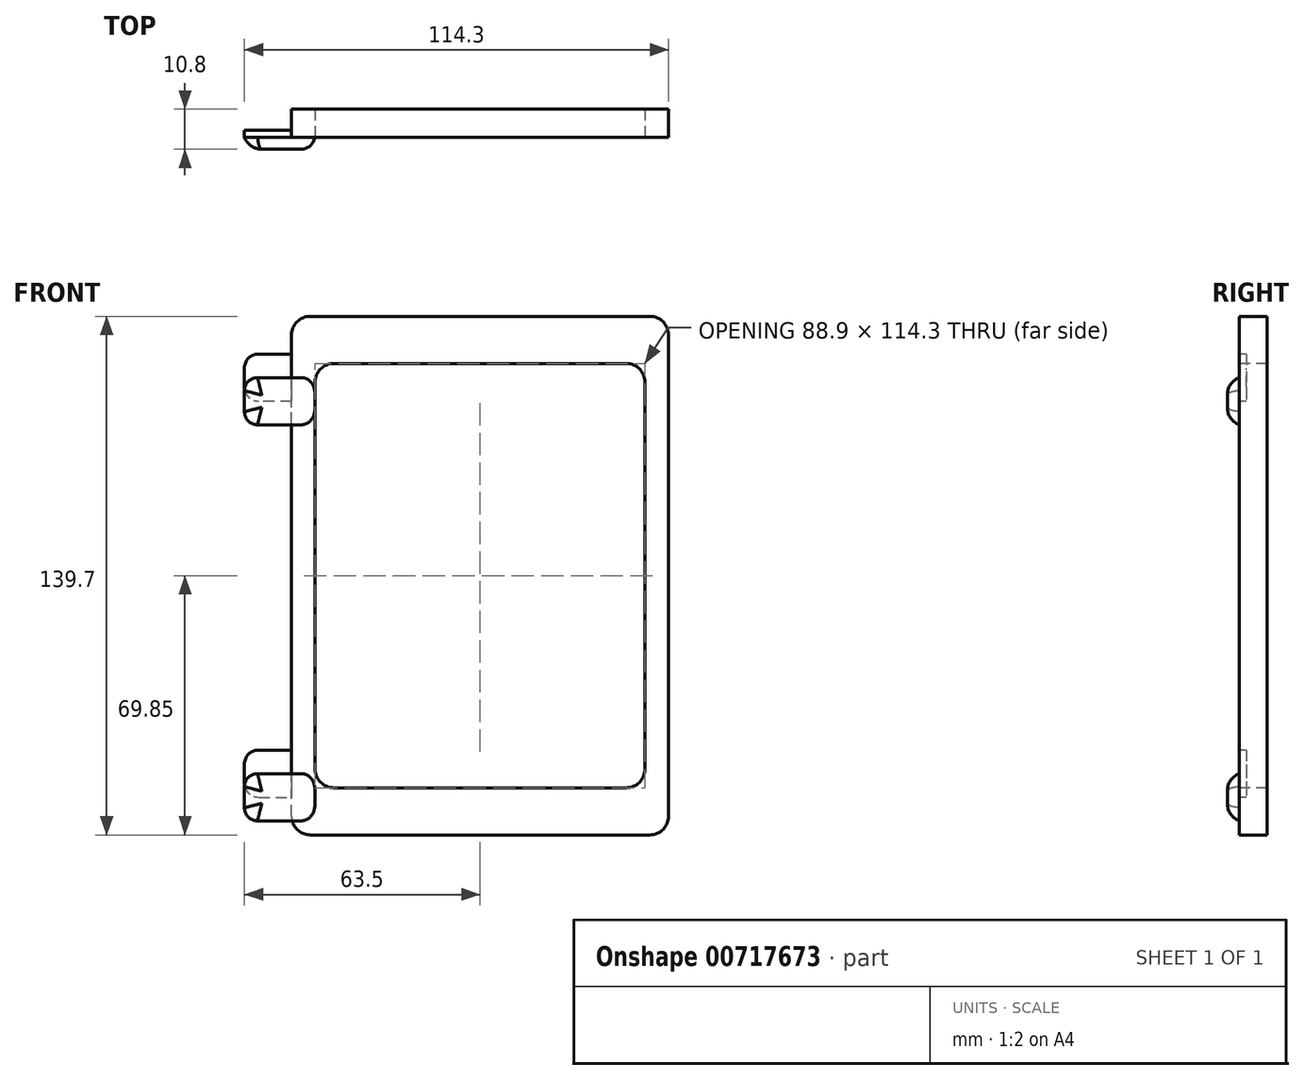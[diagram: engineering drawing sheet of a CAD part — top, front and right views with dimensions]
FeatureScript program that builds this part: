
annotation { "Feature Type Name" : "Feature", "Feature Type Description" : "" }
export const myFeature = defineFeature(function(context is Context, id is Id, definition is map)
    precondition{}
    {
        {
            var Q0;
            Q0=qCreatedBy(makeId("Front.planeOp"),FACE);
            var sketch = newSketch(context, id + "F0", { "sketchPlane" : qUnion([Q0])});
            skLineSegment(sketch, "E0.bottom", {"start": v(50.8, 69.85) * mm, "end": v(-50.8, 69.85) * mm});
            skLineSegment(sketch, "E0.top", {"start": v(50.8, -69.85) * mm, "end": v(-50.8, -69.85) * mm});
            skLineSegment(sketch, "E0.left", {"start": v(50.8, 69.85) * mm, "end": v(50.8, -69.85) * mm});
            skPoint(sketch, "E0.middle", {"position": v(0, 0) * mm});
            skLineSegment(sketch, "E1.bottom", {"start": v(44.45, 57.15) * mm, "end": v(-44.45, 57.15) * mm});
            skLineSegment(sketch, "E1.top", {"start": v(44.45, -57.15) * mm, "end": v(-44.45, -57.15) * mm});
            skLineSegment(sketch, "E1.left", {"start": v(44.45, 57.15) * mm, "end": v(44.45, -57.15) * mm});
            skLineSegment(sketch, "E2.bottom", {"start": v(-50.8, 47) * mm, "end": v(-63.5, 47) * mm});
            skLineSegment(sketch, "E2.top", {"start": v(-50.8, 59.7) * mm, "end": v(-63.5, 59.7) * mm});
            skLineSegment(sketch, "E2.right", {"start": v(-63.5, 47) * mm, "end": v(-63.5, 59.7) * mm});
            skLineSegment(sketch, "E3.bottom", {"start": v(-63.5, -46.99) * mm, "end": v(-50.8, -46.99) * mm});
            skLineSegment(sketch, "E3.top", {"start": v(-63.5, -59.69) * mm, "end": v(-50.8, -59.69) * mm});
            skPoint(sketch, "E4", {"position": v(-57.15, 53.34) * mm});
            skPoint(sketch, "E5", {"position": v(-57.15, -53.34) * mm});
            skLineSegment(sketch, "E6", {"start": v(-50.8, 59.7) * mm, "end": v(-50.8, 69.85) * mm});
            skLineSegment(sketch, "E7", {"start": v(-50.8, 47) * mm, "end": v(-50.8, -46.99) * mm});
            skLineSegment(sketch, "E8", {"start": v(-50.8, -59.69) * mm, "end": v(-50.8, -69.85) * mm});
            skLineSegment(sketch, "E9", {"start": v(-44.45, 57.15) * mm, "end": v(-44.45, -57.15) * mm});
            skLineSegment(sketch, "E10.bottom", {"start": v(-63.5, 59.7) * mm, "end": v(-45.72, 59.7) * mm});
            skLineSegment(sketch, "E10.top", {"start": v(-50.8, 47) * mm, "end": v(-45.72, 47) * mm});
            skLineSegment(sketch, "E10.right", {"start": v(-45.72, 59.7) * mm, "end": v(-45.72, 47) * mm});
            skLineSegment(sketch, "E11.bottom", {"start": v(-63.5, -46.99) * mm, "end": v(-45.72, -46.99) * mm});
            skLineSegment(sketch, "E11.top", {"start": v(-63.5, -59.69) * mm, "end": v(-45.72, -59.69) * mm});
            skLineSegment(sketch, "E11.left", {"start": v(-63.5, -46.99) * mm, "end": v(-63.5, -59.69) * mm});
            skLineSegment(sketch, "E11.right", {"start": v(-45.72, -46.99) * mm, "end": v(-45.72, -59.69) * mm});
            skLineSegment(sketch, "E12", {"start": v(-50.8, 59.7) * mm, "end": v(-50.8, 47) * mm});
            skLineSegment(sketch, "E13", {"start": v(-50.8, -46.99) * mm, "end": v(-50.8, -59.69) * mm});
            skSolve(sketch);
        }
        {
            var Q0;
            Q0=makeQuery(id+"F0.imprint","IMPRINT",FACE,{"disambiguationData":[TD([[makeQuery(id+"F0.imprint","IMPRINT",EDGE,{"derivedFrom":sQuery(id+"F0.wireOp",EDGE,"E0.bottom")}),1.0]])]});
            var Q1;
            {var subQ2=sQuery(id+"F0.wireOp",EDGE,"E10.right");Q1=makeQuery(id+"F0.imprint","IMPRINT",FACE,{"disambiguationData":[TD([[makeQuery(id+"F0.imprint","IMPRINT",EDGE,{"derivedFrom":subQ2}),-1.0]])]});}
            var Q2;
            {var subQ2=sQuery(id+"F0.wireOp",EDGE,"E11.right");Q2=makeQuery(id+"F0.imprint","IMPRINT",FACE,{"disambiguationData":[TD([[makeQuery(id+"F0.imprint","IMPRINT",EDGE,{"derivedFrom":subQ2}),-1.0]])]});}
            extrude(context, id + "F1", {"entities" : qUnion([Q0, Q1, Q2]), "depth" : -7.62 * mm, "offsetDistance" : 25.4 * mm});
        }
        {
            var Q0;
            {var subQ0=sQuery(id+"F0.wireOp",EDGE,"E2.right");Q0=makeQuery(id+"F0.imprint","IMPRINT",FACE,{"disambiguationData":[TD([[makeQuery(id+"F0.imprint","IMPRINT",EDGE,{"derivedFrom":subQ0}),-1.0]])]});}
            var Q1;
            {var subQ2=sQuery(id+"F0.wireOp",EDGE,"E11.left");Q1=makeQuery(id+"F0.imprint","IMPRINT",FACE,{"disambiguationData":[TD([[makeQuery(id+"F0.imprint","IMPRINT",EDGE,{"derivedFrom":subQ2}),1.0]])]});}
            extrude(context, id + "F2", {"entities" : qUnion([Q0, Q1]), "depth" : -1.9 * mm, "offsetDistance" : 25.4 * mm});
        }
        {
            var Q0;
            Q0=sQuery(id+"F0.wireOp",VERTEX,"E4");
            var Q1;
            Q1=sQuery(id+"F0.wireOp",VERTEX,"E5");
            var Q2;
            Q2=makeQuery(id+"F2.opExtrude","SWEPT_BODY",BODY,{"disambiguationData":[OSD([sQuery(id+"F0.wireOp",EDGE,"E2.right"),sQuery(id+"F0.wireOp",EDGE,"E10.bottom"),sQuery(id+"F0.wireOp",EDGE,"E10.top"),sQuery(id+"F0.wireOp",EDGE,"E12")])]});
            var Q3;
            Q3=makeQuery(id+"F2.opExtrude","SWEPT_BODY",BODY,{"disambiguationData":[OSD([sQuery(id+"F0.wireOp",EDGE,"E11.bottom"),sQuery(id+"F0.wireOp",EDGE,"E11.top"),sQuery(id+"F0.wireOp",EDGE,"E11.left"),sQuery(id+"F0.wireOp",EDGE,"E13")])]});
            hole(context, id + "F3", {"style" : HoleStyle.SIMPLE, "endStyle" : HoleEndStyle.THROUGH, "oppositeDirection" : true, "holeDiameter" : 2.97 * mm, "majorDiameter" : 6.35 * mm, "isTappedThrough" : true, "tappedDepth" : 12.7 * mm, "tapClearance" : 3, "locations" : qUnion([Q0, Q1]), "scope" : qUnion([Q2, Q3])});
        }
        {
            var Q0;
            Q0=makeQuery(id+"F1.opExtrude","SWEPT_EDGE",EDGE,{"disambiguationData":[OSD([sQuery(id+"F0.wireOp",EDGE,"E0.bottom"),sQuery(id+"F0.wireOp",EDGE,"E0.left")])]});
            var Q1;
            Q1=makeQuery(id+"F1.opExtrude","SWEPT_EDGE",EDGE,{"disambiguationData":[OSD([sQuery(id+"F0.wireOp",EDGE,"E0.top"),sQuery(id+"F0.wireOp",EDGE,"E0.left")])]});
            var Q2;
            Q2=makeQuery(id+"F1.opExtrude","SWEPT_EDGE",EDGE,{"disambiguationData":[OSD([sQuery(id+"F0.wireOp",EDGE,"E0.bottom"),sQuery(id+"F0.wireOp",EDGE,"E0.right")])]});
            var Q3;
            Q3=makeQuery(id+"F1.opExtrude","SWEPT_EDGE",EDGE,{"disambiguationData":[OSD([sQuery(id+"F0.wireOp",EDGE,"E0.top"),sQuery(id+"F0.wireOp",EDGE,"E0.right")])]});
            fillet(context, id + "F4", {"entities" : qUnion([Q0, Q1, Q2, Q3]), "radius" : 5.08 * mm, "tangentPropagation" : true, "allowEdgeOverflow" : false});
        }
        {
            var Q0;
            Q0=makeQuery(id+"F2.opExtrude","SWEPT_EDGE",EDGE,{"disambiguationData":[OSD([sQuery(id+"F0.wireOp",EDGE,"E2.right"),sQuery(id+"F0.wireOp",EDGE,"E10.bottom")])]});
            var Q1;
            Q1=makeQuery(id+"F2.opExtrude","SWEPT_EDGE",EDGE,{"disambiguationData":[OSD([sQuery(id+"F0.wireOp",EDGE,"E2.right"),sQuery(id+"F0.wireOp",EDGE,"E10.top")])]});
            var Q2;
            Q2=makeQuery(id+"F2.opExtrude","SWEPT_EDGE",EDGE,{"disambiguationData":[OSD([sQuery(id+"F0.wireOp",EDGE,"E11.bottom"),sQuery(id+"F0.wireOp",EDGE,"E11.left")])]});
            var Q3;
            Q3=makeQuery(id+"F2.opExtrude","SWEPT_EDGE",EDGE,{"disambiguationData":[OSD([sQuery(id+"F0.wireOp",EDGE,"E11.top"),sQuery(id+"F0.wireOp",EDGE,"E11.left")])]});
            fillet(context, id + "F5", {"entities" : qUnion([Q0, Q1, Q2, Q3]), "radius" : 3.8 * mm, "tangentPropagation" : true, "allowEdgeOverflow" : false});
        }
        {
            var Q0;
            Q0=makeQuery(id+"F1.opExtrude","SWEPT_EDGE",EDGE,{"disambiguationData":[OSD([sQuery(id+"F0.wireOp",EDGE,"E1.bottom"),sQuery(id+"F0.wireOp",EDGE,"E1.right")])]});
            var Q1;
            Q1=makeQuery(id+"F1.opExtrude","SWEPT_EDGE",EDGE,{"disambiguationData":[OSD([sQuery(id+"F0.wireOp",EDGE,"E1.top"),sQuery(id+"F0.wireOp",EDGE,"E1.right")])]});
            var Q2;
            Q2=makeQuery(id+"F1.opExtrude","SWEPT_EDGE",EDGE,{"disambiguationData":[OSD([sQuery(id+"F0.wireOp",EDGE,"E1.bottom"),sQuery(id+"F0.wireOp",EDGE,"E1.left")])]});
            var Q3;
            Q3=makeQuery(id+"F1.opExtrude","SWEPT_EDGE",EDGE,{"disambiguationData":[OSD([sQuery(id+"F0.wireOp",EDGE,"E1.top"),sQuery(id+"F0.wireOp",EDGE,"E1.left")])]});
            fillet(context, id + "F6", {"entities" : qUnion([Q0, Q1, Q2, Q3]), "radius" : 5.08 * mm, "tangentPropagation" : true, "allowEdgeOverflow" : false});
        }
        {
            var Q0;
            Q0=qCreatedBy(makeId("Front.planeOp"),FACE);
            var sketch = newSketch(context, id + "F7", { "sketchPlane" : qUnion([Q0])});
            skLineSegment(sketch, "E14.bottom", {"start": v(-63.5, 53.34) * mm, "end": v(-44.45, 53.34) * mm});
            skLineSegment(sketch, "E14.top", {"start": v(-63.5, 40.64) * mm, "end": v(-44.45, 40.64) * mm});
            skLineSegment(sketch, "E14.left", {"start": v(-63.5, 53.34) * mm, "end": v(-63.5, 40.64) * mm});
            skLineSegment(sketch, "E14.right", {"start": v(-44.45, 53.34) * mm, "end": v(-44.45, 40.64) * mm});
            skLineSegment(sketch, "E15.bottom", {"start": v(-63.5, -53.34) * mm, "end": v(-44.45, -53.34) * mm});
            skLineSegment(sketch, "E15.top", {"start": v(-63.5, -66.04) * mm, "end": v(-44.45, -66.04) * mm});
            skLineSegment(sketch, "E15.left", {"start": v(-63.5, -53.34) * mm, "end": v(-63.5, -66.04) * mm});
            skLineSegment(sketch, "E15.right", {"start": v(-44.45, -53.34) * mm, "end": v(-44.45, -66.04) * mm});
            skPoint(sketch, "E16", {"position": v(-57.15, 53.34) * mm});
            skPoint(sketch, "E17", {"position": v(-57.15, -59.69) * mm});
            skSolve(sketch);
        }
        {
            var Q0;
            Q0=makeQuery(id+"F7.imprint","IMPRINT",FACE,{"disambiguationData":[TD([[makeQuery(id+"F7.imprint","IMPRINT",EDGE,{"derivedFrom":sQuery(id+"F7.wireOp",EDGE,"E15.bottom")}),-1.0]])]});
            var Q1;
            Q1=makeQuery(id+"F7.imprint","IMPRINT",FACE,{"disambiguationData":[TD([[makeQuery(id+"F7.imprint","IMPRINT",EDGE,{"derivedFrom":sQuery(id+"F7.wireOp",EDGE,"E14.bottom")}),-1.0]])]});
            extrude(context, id + "F8", {"entities" : qUnion([Q0, Q1]), "depth" : 3.17 * mm, "offsetDistance" : 25.4 * mm});
        }
        {
            var Q0;
            Q0=makeQuery(id+"F8.opExtrude","CAP_EDGE",EDGE,{"disambiguationData":[OSD([sQuery(id+"F7.wireOp",EDGE,"E14.left")])],"isStart":false});
            var Q1;
            Q1=makeQuery(id+"F8.opExtrude","CAP_EDGE",EDGE,{"disambiguationData":[OSD([sQuery(id+"F7.wireOp",EDGE,"E14.bottom")])],"isStart":false});
            var Q2;
            Q2=makeQuery(id+"F8.opExtrude","CAP_EDGE",EDGE,{"disambiguationData":[OSD([sQuery(id+"F7.wireOp",EDGE,"E14.top")])],"isStart":false});
            var Q3;
            Q3=makeQuery(id+"F8.opExtrude","CAP_EDGE",EDGE,{"disambiguationData":[OSD([sQuery(id+"F7.wireOp",EDGE,"E15.bottom")])],"isStart":false});
            var Q4;
            Q4=makeQuery(id+"F8.opExtrude","CAP_EDGE",EDGE,{"disambiguationData":[OSD([sQuery(id+"F7.wireOp",EDGE,"E15.left")])],"isStart":false});
            var Q5;
            Q5=makeQuery(id+"F8.opExtrude","CAP_EDGE",EDGE,{"disambiguationData":[OSD([sQuery(id+"F7.wireOp",EDGE,"E15.top")])],"isStart":false});
            fillet(context, id + "F9", {"entities" : qUnion([Q0, Q1, Q2, Q3, Q4, Q5]), "radius" : 5.08 * mm, "tangentPropagation" : true, "allowEdgeOverflow" : false});
        }
        {
            var Q0;
            Q0=makeQuery(id+"F9.opFillet","BLEND_EDGE",EDGE,{"blendedFrom":[makeQuery(id+"F8.opExtrude","CAP_EDGE",EDGE,{"disambiguationData":[OSD([sQuery(id+"F7.wireOp",EDGE,"E14.bottom")])],"isStart":false}),makeQuery(id+"F8.opExtrude","CAP_EDGE",EDGE,{"disambiguationData":[OSD([sQuery(id+"F7.wireOp",EDGE,"E14.left")])],"isStart":false})],"blendedInto":[]});
            var Q1;
            Q1=makeQuery(id+"F9.opFillet","BLEND_EDGE",EDGE,{"blendedFrom":[makeQuery(id+"F8.opExtrude","CAP_EDGE",EDGE,{"disambiguationData":[OSD([sQuery(id+"F7.wireOp",EDGE,"E14.top")])],"isStart":false}),makeQuery(id+"F8.opExtrude","CAP_EDGE",EDGE,{"disambiguationData":[OSD([sQuery(id+"F7.wireOp",EDGE,"E14.left")])],"isStart":false})],"blendedInto":[]});
            var Q2;
            Q2=makeQuery(id+"F9.opFillet","BLEND_EDGE",EDGE,{"blendedFrom":[makeQuery(id+"F8.opExtrude","CAP_EDGE",EDGE,{"disambiguationData":[OSD([sQuery(id+"F7.wireOp",EDGE,"E15.bottom")])],"isStart":false}),makeQuery(id+"F8.opExtrude","CAP_EDGE",EDGE,{"disambiguationData":[OSD([sQuery(id+"F7.wireOp",EDGE,"E15.left")])],"isStart":false})],"blendedInto":[]});
            var Q3;
            Q3=makeQuery(id+"F9.opFillet","BLEND_EDGE",EDGE,{"blendedFrom":[makeQuery(id+"F8.opExtrude","CAP_EDGE",EDGE,{"disambiguationData":[OSD([sQuery(id+"F7.wireOp",EDGE,"E15.top")])],"isStart":false}),makeQuery(id+"F8.opExtrude","CAP_EDGE",EDGE,{"disambiguationData":[OSD([sQuery(id+"F7.wireOp",EDGE,"E15.left")])],"isStart":false})],"blendedInto":[]});
            fillet(context, id + "F10", {"entities" : qUnion([Q0, Q1, Q2, Q3]), "radius" : 3.8 * mm, "tangentPropagation" : true, "allowEdgeOverflow" : false});
        }
        {
            var Q0;
            Q0=makeQuery(id+"F8.opExtrude","CAP_EDGE",EDGE,{"disambiguationData":[OSD([sQuery(id+"F7.wireOp",EDGE,"E14.right")])],"isStart":false});
            var Q1;
            Q1=makeQuery(id+"F8.opExtrude","CAP_EDGE",EDGE,{"disambiguationData":[OSD([sQuery(id+"F7.wireOp",EDGE,"E15.right")])],"isStart":false});
            fillet(context, id + "F11", {"entities" : qUnion([Q0, Q1]), "radius" : 3.8 * mm, "tangentPropagation" : true, "allowEdgeOverflow" : false});
        }
    });
